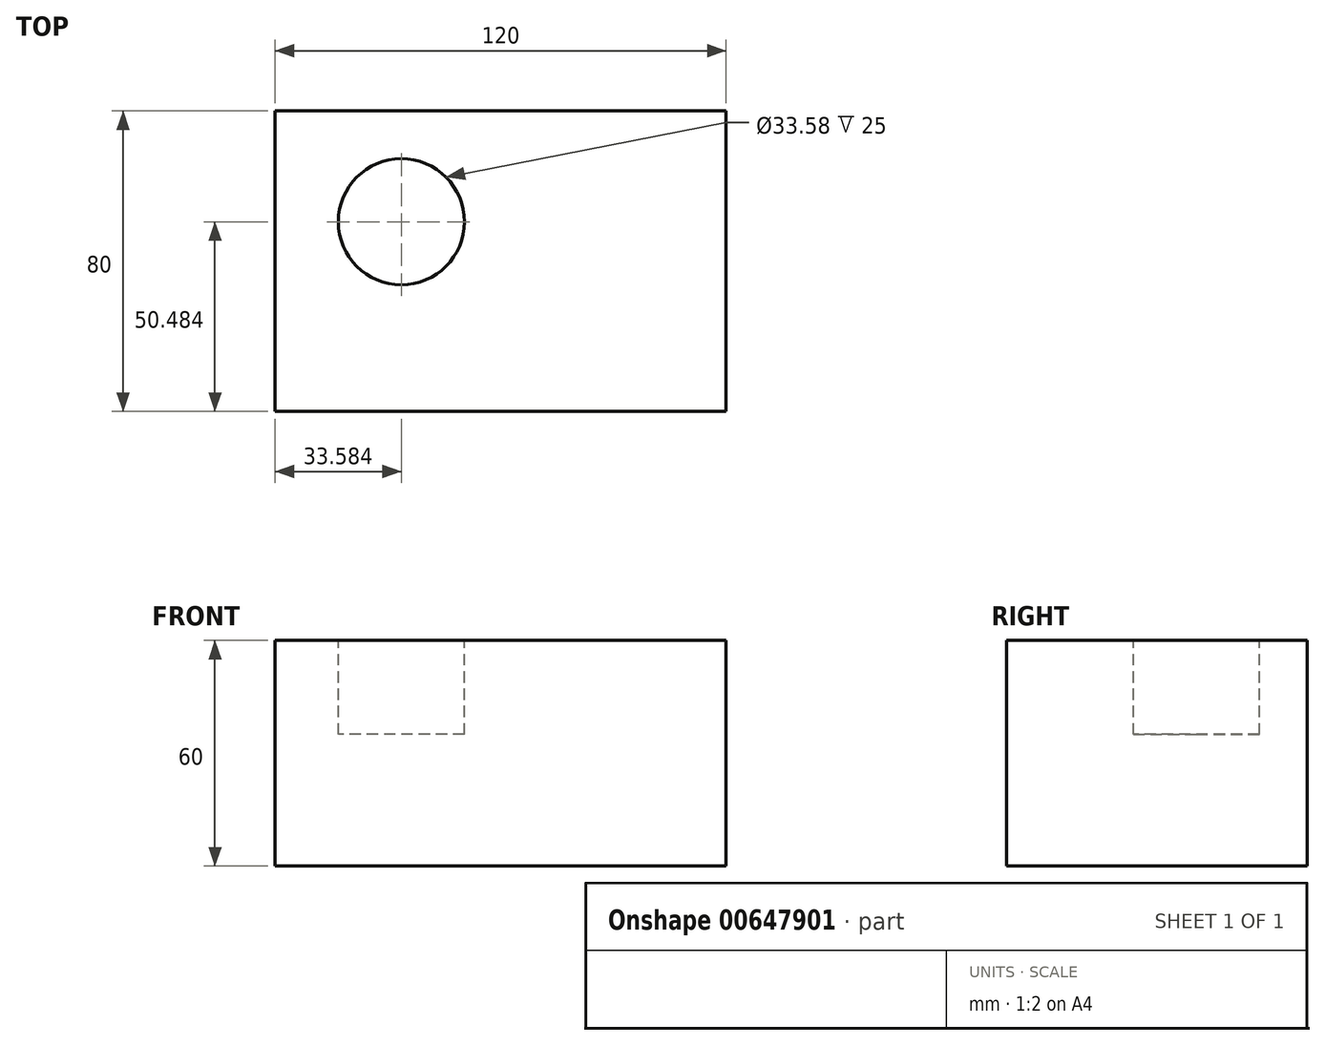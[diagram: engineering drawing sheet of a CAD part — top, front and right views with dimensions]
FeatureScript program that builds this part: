
annotation { "Feature Type Name" : "Feature", "Feature Type Description" : "" }
export const myFeature = defineFeature(function(context is Context, id is Id, definition is map)
    precondition{}
    {
        {
            var Q0;
            Q0=qCreatedBy(makeId("Top.planeOp"),FACE);
            var sketch = newSketch(context, id + "F0", { "sketchPlane" : qUnion([Q0])});
            skLineSegment(sketch, "E0.bottom", {"start": v(60, -40) * mm, "end": v(-60, -40) * mm});
            skLineSegment(sketch, "E0.top", {"start": v(60, 40) * mm, "end": v(-60, 40) * mm});
            skLineSegment(sketch, "E0.left", {"start": v(60, -40) * mm, "end": v(60, 40) * mm});
            skLineSegment(sketch, "E0.right", {"start": v(-60, -40) * mm, "end": v(-60, 40) * mm});
            skPoint(sketch, "E0.middle", {"position": v(0, 0) * mm});
            skSolve(sketch);
        }
        {
            var Q0;
            Q0 = qSketchRegion(id + "F0", true);
            extrude(context, id + "F1", {"entities" : qUnion([Q0]), "depth" : 60 * mm, "offsetDistance" : 25 * mm});
        }
        {
            var Q0;
            Q0=makeQuery(id+"F1.opExtrude","CAP_FACE",FACE,{"disambiguationData":[OSD([sQuery(id+"F0.wireOp",EDGE,"E0.bottom"),sQuery(id+"F0.wireOp",EDGE,"E0.top"),sQuery(id+"F0.wireOp",EDGE,"E0.left"),sQuery(id+"F0.wireOp",EDGE,"E0.right")])],"isStart":false});
            var sketch = newSketch(context, id + "F2", { "sketchPlane" : qUnion([Q0])});
            skCircle(sketch, "E1", {"center": v(-26.42, 10.48) * mm, "radius": 16.8 * mm});
            skLineSegment(sketch, "E2", {"start": v(-26.42, 10.48) * mm, "end": v(-26.42, -40) * mm, "construction": true});
            skLineSegment(sketch, "E3", {"start": v(-26.42, 10.48) * mm, "end": v(60, 10.48) * mm, "construction": true});
            skLineSegment(sketch, "E4", {"start": v(60, 10.48) * mm, "end": v(15.44, 40) * mm, "construction": true});
            skLineSegment(sketch, "E5", {"start": v(15.44, 40) * mm, "end": v(-26.42, 10.48) * mm, "construction": true});
            skSolve(sketch);
        }
        {
            var Q0;
            Q0=makeQuery(id+"F2.imprint","IMPRINT",FACE,{"disambiguationData":[TD([[makeQuery(id+"F2.imprint","IMPRINT",EDGE,{"derivedFrom":sQuery(id+"F2.wireOp",EDGE,"E1")}),1.0]])]});
            var Q1;
            Q1=sQuery(id+"F2.wireOp",EDGE,"E3");
            var Q2;
            Q2=sQuery(id+"F2.wireOp",EDGE,"E4");
            var Q3;
            Q3=sQuery(id+"F2.wireOp",EDGE,"E5");
            var Q4;
            Q4=sQuery(id+"F2.wireOp",EDGE,"E1");
            extrude(context, id + "F3", {"entities" : qUnion([Q0]), "operationType" : NewBodyOperationType.REMOVE, "surfaceEntities" : qUnion([Q1, Q2, Q3, Q4]), "oppositeDirection" : true, "depth" : 25 * mm, "offsetDistance" : 25 * mm});
        }
    });
